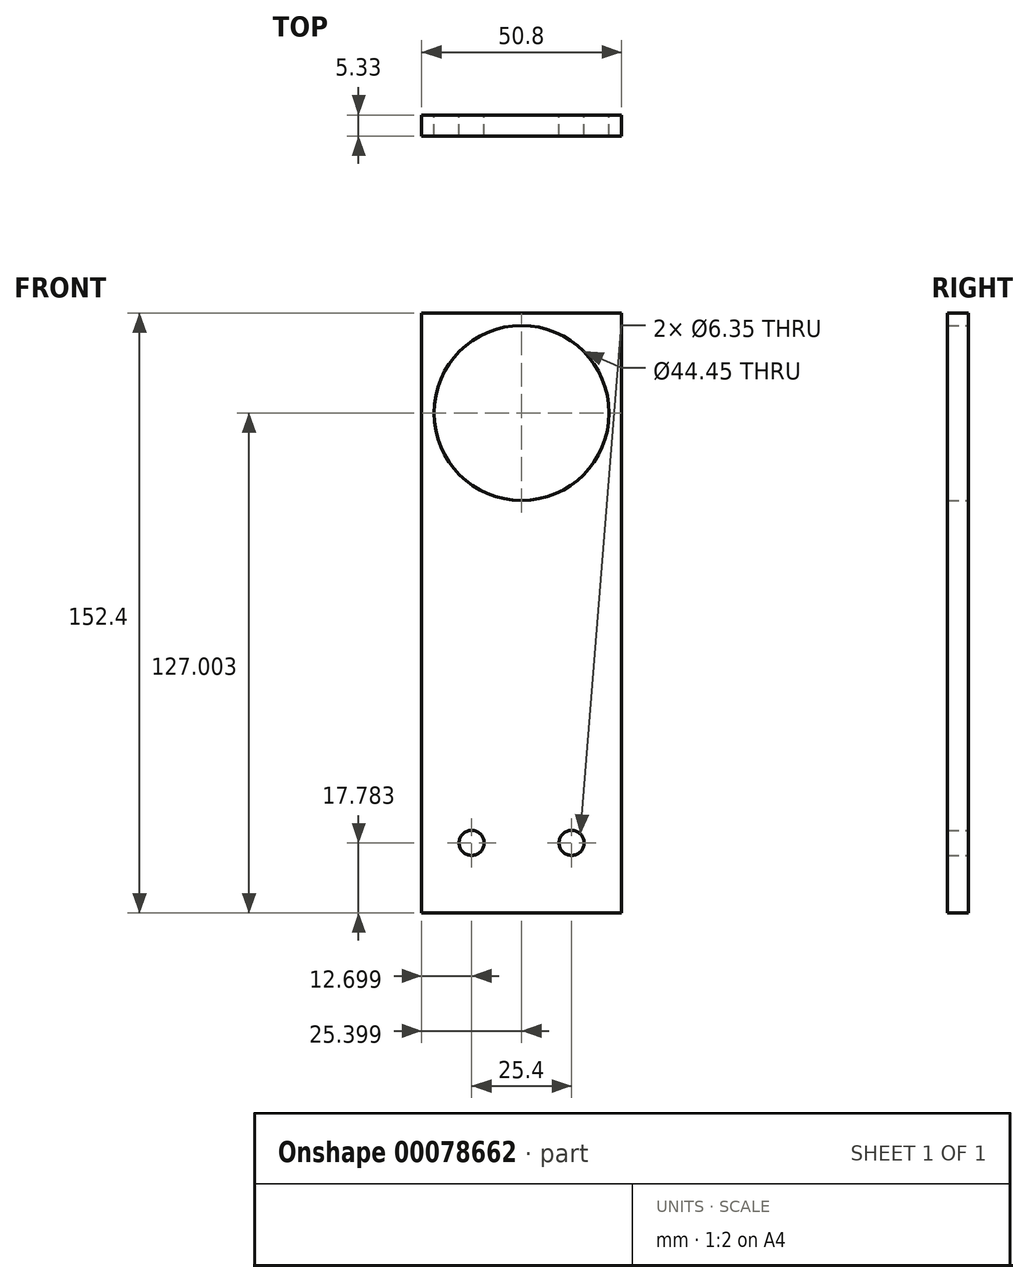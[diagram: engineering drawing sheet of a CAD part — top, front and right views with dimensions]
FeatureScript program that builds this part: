
annotation { "Feature Type Name" : "Feature", "Feature Type Description" : "" }
export const myFeature = defineFeature(function(context is Context, id is Id, definition is map)
    precondition{}
    {
        {
            var Q0;
            Q0=qCreatedBy(makeId("Front.planeOp"),FACE);
            var sketch = newSketch(context, id + "F0", { "sketchPlane" : qUnion([Q0])});
            skLineSegment(sketch, "E0.bottom", {"start": v(-116.85, 97.64) * mm, "end": v(-66.05, 97.64) * mm});
            skLineSegment(sketch, "E0.top", {"start": v(-116.85, -54.76) * mm, "end": v(-66.05, -54.76) * mm});
            skLineSegment(sketch, "E0.left", {"start": v(-116.85, 97.64) * mm, "end": v(-116.85, -54.76) * mm});
            skLineSegment(sketch, "E0.right", {"start": v(-66.05, 97.64) * mm, "end": v(-66.05, -54.76) * mm});
            skCircle(sketch, "E1", {"center": v(-104.15, -36.98) * mm, "radius": 3.18 * mm});
            skCircle(sketch, "E2", {"center": v(-78.75, -36.98) * mm, "radius": 3.18 * mm});
            skCircle(sketch, "E3", {"center": v(-91.45, 72.24) * mm, "radius": 22.23 * mm});
            skPoint(sketch, "E3.centerSnap0", {"position": v(-91.45, 97.64) * mm});
            skSolve(sketch);
        }
        {
            var Q0;
            Q0=makeQuery(id+"F0.imprint","IMPRINT",FACE,{"disambiguationData":[TD([[makeQuery(id+"F0.imprint","IMPRINT",EDGE,{"derivedFrom":sQuery(id+"F0.wireOp",EDGE,"E0.bottom")}),-1.0]])]});
            extrude(context, id + "F1", {"entities" : qUnion([Q0]), "depth" : 5.33 * mm});
        }
    });
